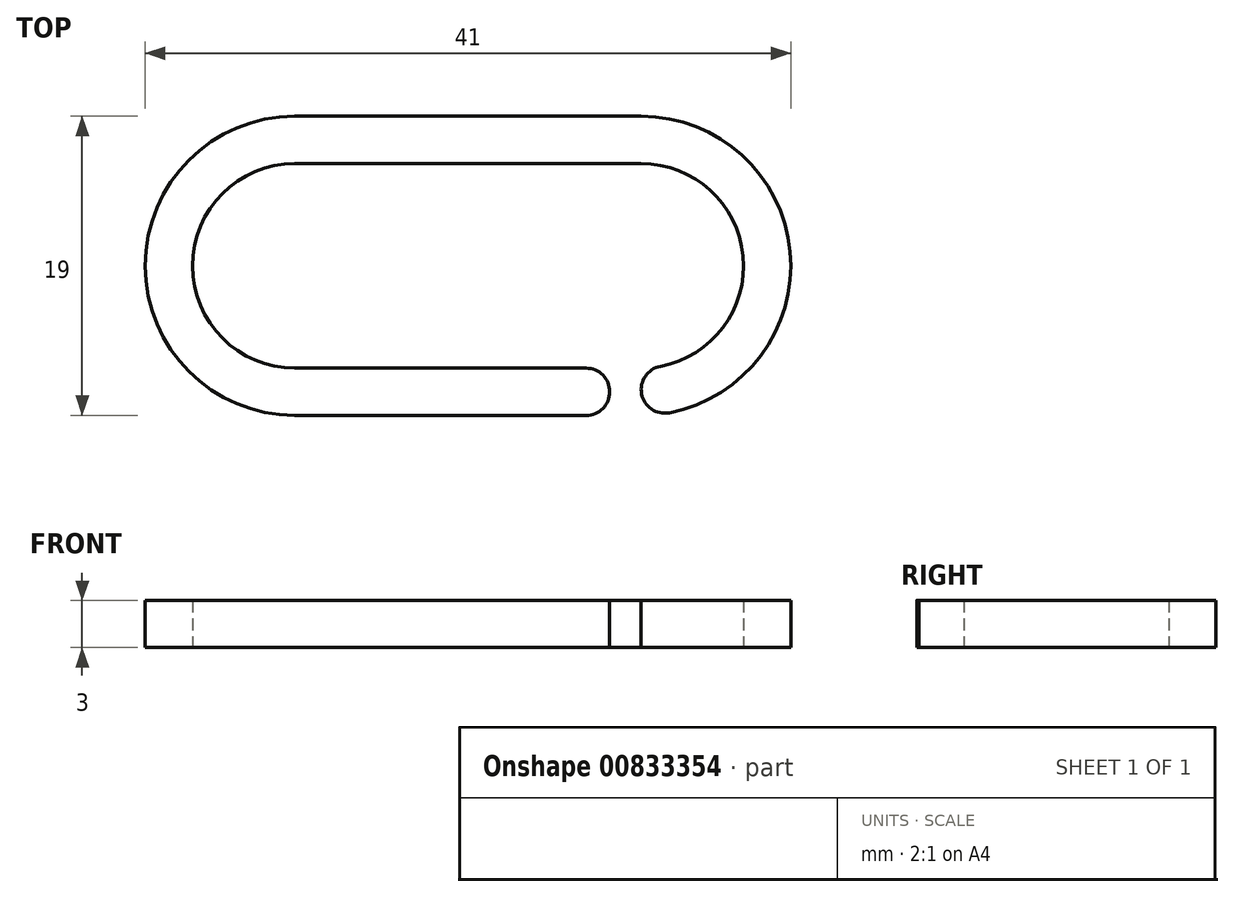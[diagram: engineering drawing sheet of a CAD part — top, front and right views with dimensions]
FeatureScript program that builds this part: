
annotation { "Feature Type Name" : "Feature", "Feature Type Description" : "" }
export const myFeature = defineFeature(function(context is Context, id is Id, definition is map)
    precondition{}
    {
        {
            var Q0;
            Q0=qCreatedBy(makeId("Top.planeOp"),FACE);
            var sketch = newSketch(context, id + "F0", { "sketchPlane" : qUnion([Q0])});
            skArc(sketch, "E0", {"start": v(0, 6.5) * mm, "mid": v(-6.5, 0) * mm, "end": v(0, -6.5) * mm});
            skArc(sketch, "E1", {"start": v(22, -6.5) * mm, "mid": v(28.5, 0) * mm, "end": v(22, 6.5) * mm});
            skPoint(sketch, "E2", {"position": v(-6.5, 0) * mm});
            skPoint(sketch, "E3", {"position": v(28.5, 0) * mm});
            skLineSegment(sketch, "E4", {"start": v(0, 6.5) * mm, "end": v(22, 6.5) * mm});
            skLineSegment(sketch, "E5", {"start": v(0, -6.5) * mm, "end": v(22, -6.5) * mm});
            skLineSegment(sketch, "E6.0", {"start": v(0, 9.5) * mm, "end": v(22, 9.5) * mm});
            skArc(sketch, "E6.1", {"start": v(0, 9.5) * mm, "mid": v(-9.5, 0) * mm, "end": v(0, -9.5) * mm});
            skLineSegment(sketch, "E6.2", {"start": v(0, -9.5) * mm, "end": v(22, -9.5) * mm});
            skArc(sketch, "E6.3", {"start": v(22, -9.5) * mm, "mid": v(31.5, 0) * mm, "end": v(22, 9.5) * mm});
            skLineSegment(sketch, "E7.bottom", {"start": v(22, -6.5) * mm, "end": v(20, -6.5) * mm});
            skLineSegment(sketch, "E7.top", {"start": v(22, -9.5) * mm, "end": v(20, -9.5) * mm});
            skLineSegment(sketch, "E7.left", {"start": v(22, -6.5) * mm, "end": v(22, -9.5) * mm});
            skLineSegment(sketch, "E7.right", {"start": v(20, -6.5) * mm, "end": v(20, -9.5) * mm});
            skSolve(sketch);
        }
        {
            var Q0;
            Q0=makeQuery(id+"F0.imprint","IMPRINT",FACE,{"disambiguationData":[TD([[makeQuery(id+"F0.imprint","IMPRINT",EDGE,{"derivedFrom":sQuery(id+"F0.wireOp",EDGE,"E0")}),-1.0]])]});
            extrude(context, id + "F1", {"entities" : qUnion([Q0]), "depth" : 3 * mm, "offsetDistance" : 25 * mm});
        }
        {
            var Q0;
            Q0=makeQuery(id+"F1.opExtrude","SWEPT_EDGE",EDGE,{"disambiguationData":[OSD([sQuery(id+"F0.wireOp",EDGE,"E6.2"),sQuery(id+"F0.wireOp",EDGE,"E7.top"),sQuery(id+"F0.wireOp",EDGE,"E7.right")])]});
            var Q1;
            Q1=makeQuery(id+"F1.opExtrude","SWEPT_EDGE",EDGE,{"disambiguationData":[OSD([sQuery(id+"F0.wireOp",EDGE,"E5"),sQuery(id+"F0.wireOp",EDGE,"E7.bottom"),sQuery(id+"F0.wireOp",EDGE,"E7.right")])]});
            var Q2;
            Q2=makeQuery(id+"F1.opExtrude","SWEPT_EDGE",EDGE,{"disambiguationData":[OSD([sQuery(id+"F0.wireOp",EDGE,"E1"),sQuery(id+"F0.wireOp",EDGE,"E7.bottom"),sQuery(id+"F0.wireOp",EDGE,"E7.left")])]});
            var Q3;
            Q3=makeQuery(id+"F1.opExtrude","SWEPT_EDGE",EDGE,{"disambiguationData":[OSD([sQuery(id+"F0.wireOp",EDGE,"E6.3"),sQuery(id+"F0.wireOp",EDGE,"E7.top"),sQuery(id+"F0.wireOp",EDGE,"E7.left")])]});
            fillet(context, id + "F2", {"entities" : qUnion([Q0, Q1, Q2, Q3]), "radius" : 1.5 * mm, "tangentPropagation" : true, "allowEdgeOverflow" : false});
        }
    });
